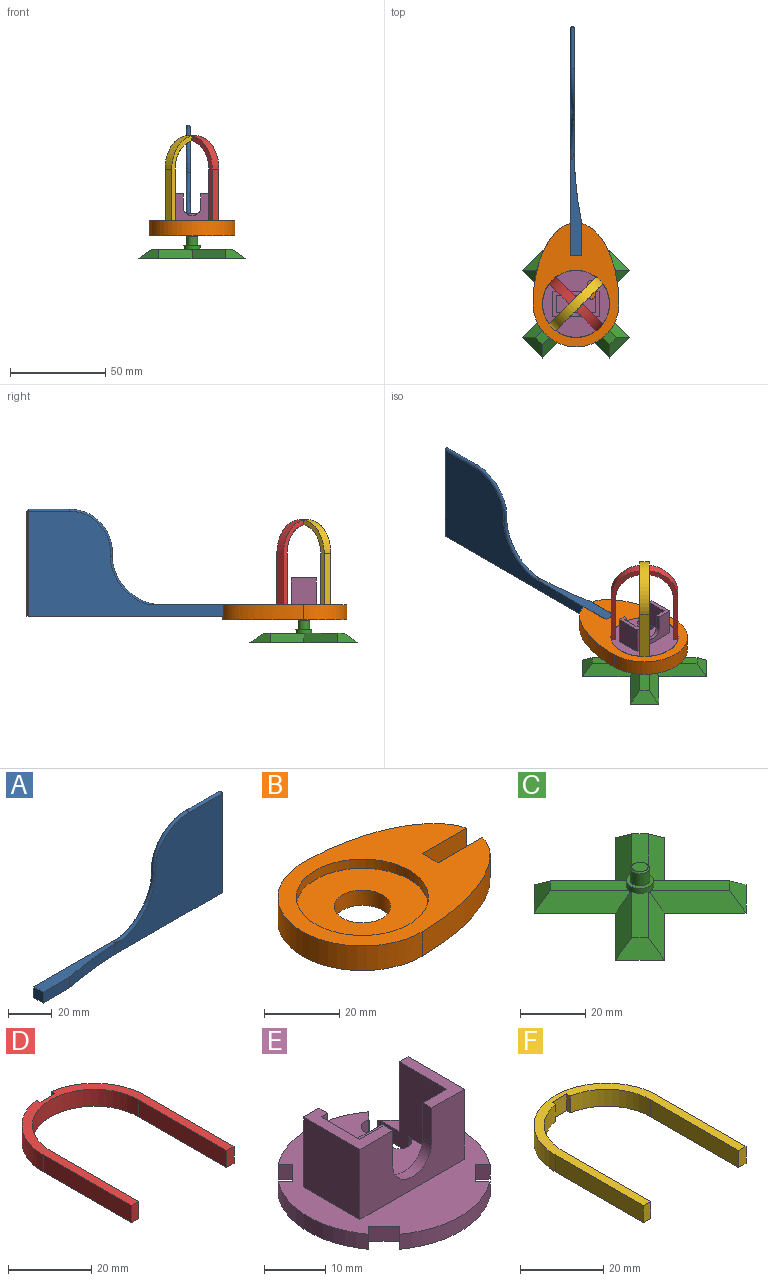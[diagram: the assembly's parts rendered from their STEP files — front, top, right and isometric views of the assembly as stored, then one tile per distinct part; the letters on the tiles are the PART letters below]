
ASSEMBLY  parts=6 mates=5
PART A: 13 faces, bbox 120x5.9x57.9 mm
  f0: plane 55.95x5.9mm, normal (0,0,1), area 218.7mm2, adj f1,f3,f4,f5,f9
  f1: plane 6x5.9mm, normal (-1,0,0), area 35.4mm2, adj f0,f2,f3,f4
  f2: plane 120x5.9mm, normal (0,0,-1), area 354.3mm2, adj f1,f3,f4,f5,f6,f10,f11
  f3: plane 17x6mm, normal (0,-1,0), area 102mm2, adj f0,f1,f2,f5
  f4: plane 119x55mm, normal (0,1,0), area 2864mm2, adj f0,f1,f2,f7,f8,f9,f10
  f5: cylinder r=200mm len=37.15mm, axis (0,0,-1), area 201.5mm2, adj f0,f2,f3,f6,f9
  f6: plane 69x55mm, normal (0,-1,0), area 2560.4mm2, adj f2,f5,f7,f8,f9,f11
  f7: cylinder r=1mm len=21.5mm, axis (1,0,0), area 67.5mm2, adj f4,f6,f8,f12
  f8: torus R=21.5mm, axis (0,-1,0), area 117.6mm2, adj f4,f6,f7,f9
  f9: torus R=27.63mm, axis (0,-1,0), area 116.5mm2, adj f0,f4,f5,f6,f8
  f10: plane 55x1mm, normal (0.71,0.71,0), area 77.8mm2, adj f2,f4,f11,f12
  f11: plane 55x1mm, normal (0.71,-0.71,0), area 77.8mm2, adj f2,f6,f10,f12
  f12: cone r=1mm half-angle=45deg, axis (-1,0,0), area 2.2mm2, adj f7,f10,f11
PART B: 11 faces, bbox 65x45x8 mm
  f0: cylinder r=22.5mm len=45mm, axis (0,0,-1), area 565.5mm2, adj f1,f2,f3
  f1: extruded ~45x42.5mm, area 799.9mm2, adj f0,f2,f3,f6,f8,f9
  f2: plane 64.62x45mm, normal (0,0,1), area 1222.9mm2, adj f0,f1,f4,f6,f7,f8
  f3: plane 65x45mm, normal (0,0,-1), area 2118.2mm2, adj f0,f1,f10
  f4: cylinder r=17.6mm len=35.2mm, axis (0,0,1), area 331.8mm2, adj f2,f5
  f5: plane 35.2x35.2mm, normal (0,0,1), area 794.1mm2, adj f4,f10
  f6: plane 16.62x6mm, normal (0,-1,0), area 99.7mm2, adj f1,f2,f7,f9
  f7: plane 6x6mm, normal (1,0,0), area 36mm2, adj f2,f6,f8,f9
  f8: plane 16.62x6mm, normal (0,1,0), area 99.7mm2, adj f1,f2,f7,f9
  f9: plane 17x6mm, normal (0,0,1), area 101.2mm2, adj f1,f6,f7,f8
  f10: cylinder r=7.55mm len=15.1mm, axis (0,0,-1), area 237.2mm2, adj f3,f5
PART C: 22 faces, bbox 56.6x56.6x12 mm
  f0: plane 20.55x20.55mm, normal (0,0,1), area 117.5mm2, adj f5,f13,f15,f17
  f1: plane 20.55x20.55mm, normal (0,0,1), area 117.5mm2, adj f5,f10,f11,f12
  f2: plane 20.55x20.55mm, normal (0,0,1), area 117.5mm2, adj f5,f14,f16,f18
  f3: plane 20.55x20.55mm, normal (0,0,1), area 117.5mm2, adj f5,f19,f20,f21
  f4: plane 56.57x56.57mm, normal (0,0,-1), area 1725mm2, adj f10,f11,f12,f13,f14,f15,f16,f17
  f5: cylinder r=4.25mm len=8.5mm, axis (0,0,-1), area 54.8mm2, adj f0,f1,f2,f3,f6,f11,f12,f13
  f6: plane 8.5x8.5mm, normal (0,0,1), area 28.5mm2, adj f5,f7
  f7: cylinder r=3mm len=6mm, axis (0,0,-1), area 84.8mm2, adj f6,f9
  f8: plane 5x5mm, normal (0,0,1), area 19.6mm2, adj f9
  f9: cone r=2.5mm half-angle=45deg, axis (0,0,-1), area 12.2mm2, adj f7,f8
  f10: plane 10.61x10.61mm, normal (0.5,0.5,0.71), area 70.7mm2, adj f1,f4,f11,f12
  f11: plane 24.1x17.69mm, normal (0.5,-0.5,0.71), area 176.4mm2, adj f1,f4,f5,f10,f13
  f12: plane 24.1x17.69mm, normal (-0.5,0.5,0.71), area 176.4mm2, adj f1,f4,f5,f10,f14
  f13: plane 24.1x17.69mm, normal (0.5,0.5,0.71), area 176.4mm2, adj f0,f4,f5,f11,f15
  f14: plane 24.1x17.69mm, normal (0.5,0.5,0.71), area 176.4mm2, adj f2,f4,f5,f12,f16
  f15: plane 10.61x10.61mm, normal (0.5,-0.5,0.71), area 70.7mm2, adj f0,f4,f13,f17
  f16: plane 10.61x10.61mm, normal (-0.5,0.5,0.71), area 70.7mm2, adj f2,f4,f14,f18
  f17: plane 24.1x17.69mm, normal (-0.5,-0.5,0.71), area 176.4mm2, adj f0,f4,f5,f15,f19
  f18: plane 24.1x17.69mm, normal (-0.5,-0.5,0.71), area 176.4mm2, adj f2,f4,f5,f16,f20
  f19: plane 24.1x17.69mm, normal (0.5,-0.5,0.71), area 176.4mm2, adj f3,f4,f5,f17,f21
  f20: plane 24.1x17.69mm, normal (-0.5,0.5,0.71), area 176.4mm2, adj f3,f4,f5,f18,f21
  f21: plane 10.61x10.61mm, normal (-0.5,-0.5,0.71), area 70.7mm2, adj f3,f4,f19,f20
PART D: 14 faces, bbox 35x47.3x5 mm
  f0: cylinder r=17.5mm len=17.31mm, axis (0,0,-1), area 124.6mm2, adj f1,f2,f6,f11
  f1: plane 47.31x35mm, normal (0,0,1), area 270.6mm2, adj f0,f3,f4,f5,f6,f7,f8,f9
  f2: plane 47.31x35mm, normal (0,0,-1), area 270.6mm2, adj f0,f3,f4,f5,f6,f7,f8,f9
  f3: cylinder r=15mm len=30mm, axis (0,0,-1), area 235.6mm2, adj f1,f2,f4,f10
  f4: plane 30x5mm, normal (-1,0,0), area 150mm2, adj f1,f2,f3,f5
  f5: plane 5x2.5mm, normal (0,-1,0), area 12.5mm2, adj f1,f2,f4,f6
  f6: plane 30x5mm, normal (1,0,0), area 150mm2, adj f0,f1,f2,f5
  f7: cylinder r=17.5mm len=17.31mm, axis (0,0,-1), area 124.6mm2, adj f1,f2,f8,f12
  f8: plane 30x5mm, normal (-1,0,0), area 150mm2, adj f1,f2,f7,f9
  f9: plane 5x2.5mm, normal (0,-1,0), area 12.5mm2, adj f1,f2,f8,f10
  f10: plane 30x5mm, normal (1,0,0), area 150mm2, adj f1,f2,f3,f9
  f11: plane 5x1.26mm, normal (-1,0,0), area 6.3mm2, adj f0,f1,f2,f13
  f12: plane 5x1.26mm, normal (1,0,0), area 6.3mm2, adj f1,f2,f7,f13
  f13: plane 5.1x5mm, normal (0,1,0), area 25.5mm2, adj f1,f2,f11,f12
PART E: 40 faces, bbox 35x35x17 mm
  f0: cylinder r=17.5mm len=20.96mm, axis (0,0,1), area 67.4mm2, adj f4,f7,f28,f37
  f1: cylinder r=17.5mm len=20.96mm, axis (0,0,1), area 67.4mm2, adj f4,f7,f32,f36
  f2: cylinder r=17.5mm len=20.96mm, axis (0,0,1), area 67.4mm2, adj f4,f7,f30,f38
  f3: cylinder r=17.5mm len=20.96mm, axis (0,0,1), area 67.4mm2, adj f4,f7,f27,f34
  f4: plane 35x35mm, normal (0,0,1), area 577.8mm2, adj f0,f1,f2,f3,f5,f6,f11,f13
  f5: cylinder r=2mm len=3mm, axis (0,0,1), area 2.7mm2, adj f4,f7,f13,f33
  f6: plane 18.1x14mm, normal (0,1,0), area 100.1mm2, adj f4,f9,f10,f15,f23,f25
  f7: plane 35x35mm, normal (0,0,-1), area 876.8mm2, adj f0,f1,f2,f3,f5,f13,f24,f25
  f8: plane 16.1x14mm, normal (0,-1,0), area 72.1mm2, adj f9,f10,f18,f19,f23,f25
  f9: plane 14.6x2mm, normal (0,0,1), area 29.2mm2, adj f6,f8,f23,f25
  f10: plane 13x7.55mm, normal (0,0,1), area 40.1mm2, adj f6,f8,f14,f15,f16,f18,f22,f23
  f11: plane 14x2mm, normal (0,1,0), area 28mm2, adj f4,f12,f13,f17
  f12: plane 13x7.55mm, normal (0,0,1), area 37.1mm2, adj f11,f13,f14,f16,f17,f21
  f13: plane 17x15mm, normal (-1,0,0), area 172mm2, adj f4,f5,f7,f11,f12,f14,f19,f26
  f14: plane 20.1x14mm, normal (0,1,0), area 186.6mm2, adj f10,f12,f13,f18,f19,f20,f21,f22
  f15: plane 14x13mm, normal (-1,0,0), area 182mm2, adj f4,f6,f10,f16
  f16: plane 24.1x14mm, normal (0,-1,0), area 242.6mm2, adj f4,f10,f12,f15,f17,f20,f21,f22
  f17: plane 14x13mm, normal (1,0,0), area 182mm2, adj f4,f11,f12,f16
  f18: plane 14x9mm, normal (1,0,0), area 126mm2, adj f8,f10,f14,f19
  f19: plane 20.1x9mm, normal (0,0,1), area 174.6mm2, adj f8,f13,f14,f18,f26
  f20: cylinder r=4.5mm len=9mm, axis (0,-1,0), area 28.3mm2, adj f14,f16,f21,f22
  f21: plane 7x2mm, normal (-1,0,0), area 14mm2, adj f12,f14,f16,f20
  f22: plane 7x2mm, normal (1,0,0), area 14mm2, adj f10,f14,f16,f20
  f23: plane 10.5x2mm, normal (1,0,0), area 21mm2, adj f6,f8,f9,f10
  f24: cylinder r=2mm len=3mm, axis (0,0,1), area 12.1mm2, adj f4,f7,f25,f31
  f25: plane 6.5x6mm, normal (1,0,0), area 25mm2, adj f4,f6,f7,f8,f9,f24,f26
  f26: cylinder r=2mm len=4mm, axis (0,0,1), area 18.8mm2, adj f7,f13,f19,f25
  f27: plane 3x1.64mm, normal (-0.71,0.71,0), area 7mm2, adj f3,f4,f7,f29
  f28: plane 3x1.64mm, normal (0.71,-0.71,0), area 7mm2, adj f0,f4,f7,f29
  f29: plane 3.54x3.54mm, normal (-0.71,-0.71,0), area 15mm2, adj f4,f7,f27,f28
  f30: plane 3x1.64mm, normal (0.71,-0.71,0), area 7mm2, adj f2,f4,f7,f31
  f31: plane 3x0.07mm, normal (0.71,0.71,0), area 0.3mm2, adj f4,f7,f24,f30
  f32: plane 3x1.64mm, normal (-0.71,0.71,0), area 7mm2, adj f1,f4,f7,f33
  f33: plane 3x2.52mm, normal (0.71,0.71,0), area 10.7mm2, adj f4,f5,f7,f32
  f34: plane 3x1.64mm, normal (0.71,0.71,0), area 7mm2, adj f3,f4,f7,f35
  f35: plane 3.54x3.54mm, normal (0.71,-0.71,0), area 15mm2, adj f4,f7,f34,f36
  f36: plane 3x1.64mm, normal (-0.71,-0.71,0), area 7mm2, adj f1,f4,f7,f35
  f37: plane 3x1.64mm, normal (0.71,0.71,0), area 7mm2, adj f0,f4,f7,f39
  f38: plane 3x1.64mm, normal (-0.71,-0.71,0), area 7mm2, adj f2,f4,f7,f39
  f39: plane 3.54x3.54mm, normal (-0.71,0.71,0), area 15mm2, adj f4,f7,f37,f38
PART F: 14 faces, bbox 35x47.5x5 mm
  f0: cylinder r=15mm len=14.79mm, axis (0,0,-1), area 105.2mm2, adj f1,f3,f10,f11
  f1: plane 47.5x35mm, normal (0,0,-1), area 272mm2, adj f0,f2,f3,f4,f5,f6,f7,f8
  f2: cylinder r=15mm len=14.79mm, axis (0,0,-1), area 105.2mm2, adj f1,f9,f10,f13
  f3: plane 30x5mm, normal (-1,0,0), area 150mm2, adj f0,f1,f4,f10
  f4: plane 5x2.5mm, normal (0,-1,0), area 12.5mm2, adj f1,f3,f5,f10
  f5: plane 30x5mm, normal (1,0,0), area 150mm2, adj f1,f4,f6,f10
  f6: cylinder r=17.5mm len=35mm, axis (0,0,-1), area 274.9mm2, adj f1,f5,f7,f10
  f7: plane 30x5mm, normal (-1,0,0), area 150mm2, adj f1,f6,f8,f10
  f8: plane 5x2.5mm, normal (0,-1,0), area 12.5mm2, adj f1,f7,f9,f10
  f9: plane 30x5mm, normal (1,0,0), area 150mm2, adj f1,f2,f8,f10
  f10: plane 47.5x35mm, normal (0,0,1), area 272mm2, adj f0,f2,f3,f4,f5,f6,f7,f8
  f11: plane 5x1.26mm, normal (-1,0,0), area 6.3mm2, adj f0,f1,f10,f12
  f12: plane 5.01x5mm, normal (0,-1,0), area 25.1mm2, adj f1,f10,f11,f13
  f13: plane 5x1.26mm, normal (1,0,0), area 6.3mm2, adj f1,f2,f10,f12
PLACE A rot(axis=(0,0,1),90deg) t=(22.8,83.37,-36.18)mm
PLACE B rot(axis=(0,0,1),90deg) t=(25.75,-2.13,-41.18)mm
PLACE C t=(25.75,-2.13,-53.18)mm
PLACE D rot(axis=(0.28,0.68,0.68),148.6deg) t=(23.98,-3.9,-36.18)mm
PLACE E t=(25.75,-2.13,-33.18)mm
PLACE F rot(axis=(0.86,0.36,0.36),98.4deg) t=(23.98,-0.36,-36.17)mm
MATE revolute B.f10 <-> C.f7  axis (0,0,-1) through (25.75,-2.13,-41.18)mm
MATE fastened B.f7 <-> A.f1  axis (0,1,0) through (25.75,23.37,-36.18)mm
MATE fastened D.f10 <-> E.f35  axis (0.71,-0.71,0) through (36.35,-12.74,-36.18)mm
MATE fastened F.f12 <-> D.f13  axis (0,0,-1) through (25.75,-2.13,9.88)mm
MATE fastened B.f4 <-> E.f0  axis (0,0,1) through (25.75,-2.13,-36.18)mm
